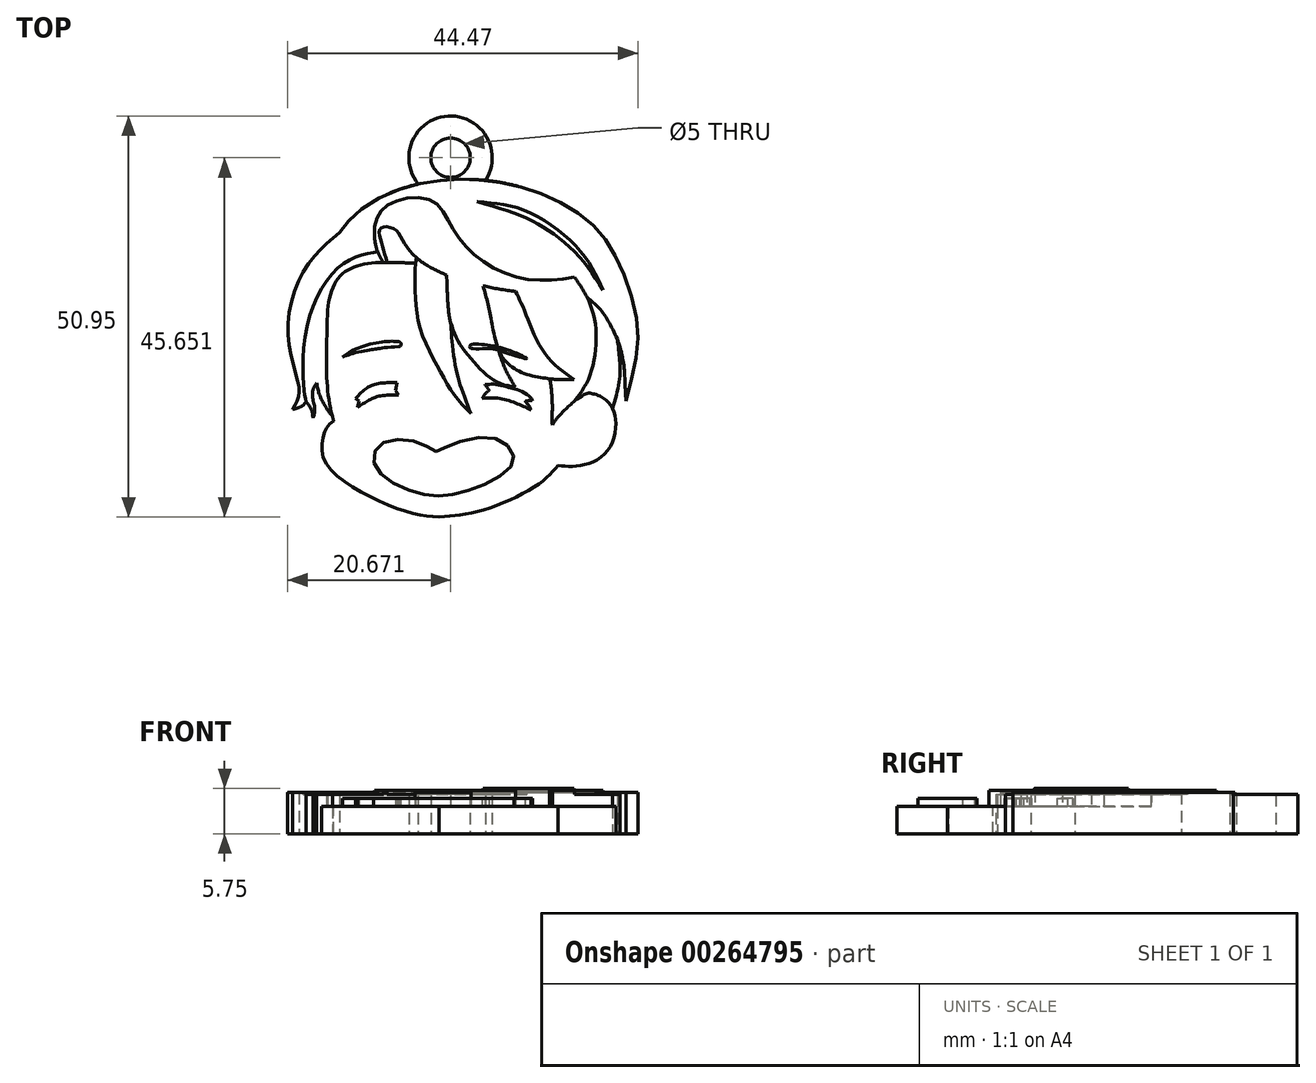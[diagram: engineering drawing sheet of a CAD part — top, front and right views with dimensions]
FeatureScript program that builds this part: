
annotation { "Feature Type Name" : "Feature", "Feature Type Description" : "" }
export const myFeature = defineFeature(function(context is Context, id is Id, definition is map)
    precondition{}
    {
        {
            var Q0;
            Q0=qCreatedBy(makeId("Top.planeOp"),FACE);
            var sketch = newSketch(context, id + "F0", { "sketchPlane" : qUnion([Q0])});
            skLineSegment(sketch, "E0", {"start": v(0, 26.14) * mm, "end": v(0, -13.86) * mm, "construction": true});
            skFitSpline(sketch, "E1", {"points": [v(-13.4, -3.41) * mm, v(-14.59, -4.9) * mm, v(-14.68, -8.16) * mm, v(-10.4, -12.17) * mm, v(-3.68, -15.06) * mm, v(0, -15.62) * mm], "startDerivative": vector(-13.93, -9.32) * mm, "endDerivative": vector(18.39, -1.5) * mm});
            skFitSpline(sketch, "E2", {"points": [v(0, -15.62) * mm, v(5.36, -14.78) * mm, v(12.63, -11.43) * mm, v(15.05, -9.1) * mm], "startDerivative": vector(14.98, 1.14) * mm, "endDerivative": vector(7.26, 8.68) * mm});
            skFitSpline(sketch, "E3", {"points": [v(15.05, -9.1) * mm, v(17.76, -9.1) * mm, v(21.2, -7.42) * mm, v(22.42, -3.41) * mm, v(21.58, -1.17) * mm, v(18.5, 0) * mm, v(15.05, -3.41) * mm, v(15.05, -4.25) * mm], "startDerivative": vector(18.97, -1.5) * mm, "endDerivative": vector(3.2, -10.24) * mm, "construction": true});
            skFitSpline(sketch, "E4", {"points": [v(14.37, -3.91) * mm, v(15.86, -2.1) * mm, v(18.5, 0) * mm, v(19.35, 0.08) * mm, v(20.48, -0.29) * mm, v(21.58, -1.17) * mm, v(22.42, -3.41) * mm, v(21.2, -7.42) * mm, v(17.76, -9.1) * mm, v(15.05, -9.1) * mm], "startDerivative": vector(9.94, 16.2) * mm, "endDerivative": vector(-21.45, 1.73) * mm});
            skFitSpline(sketch, "E5", {"points": [v(-14.19, 10.66) * mm, v(-12.54, 15.05) * mm, v(-8.76, 16.63) * mm, v(-3.04, 16.63) * mm], "startDerivative": vector(1.75, 16.5) * mm, "endDerivative": vector(16.06, -0.48) * mm});
            skFitSpline(sketch, "E6", {"points": [v(-3.04, 16.63) * mm, v(-3.04, 12.63) * mm, v(-2.33, 8) * mm, v(0, 3.15) * mm, v(1.82, 0) * mm, v(4.02, -2.5) * mm], "startDerivative": vector(-0.37, -20.1) * mm, "endDerivative": vector(13.1, -13.51) * mm});
            skFitSpline(sketch, "E7", {"points": [v(4.02, -2.5) * mm, v(2.77, 0.87) * mm, v(1.98, 3.93) * mm, v(1.56, 7.52) * mm, v(1.43, 9.09) * mm], "startDerivative": vector(-5.05, 13.03) * mm, "endDerivative": vector(-1.35, 13.2) * mm});
            skFitSpline(sketch, "E8", {"points": [v(1.43, 9.09) * mm, v(2.5, 6.55) * mm, v(4.66, 3.77) * mm, v(7.17, 1.61) * mm, v(9.69, 0.87) * mm], "startDerivative": vector(3.7, -10.7) * mm, "endDerivative": vector(11.1, -2.02) * mm});
            skFitSpline(sketch, "E9", {"points": [v(7.82, 5.39) * mm, v(9.13, 3.52) * mm, v(11.7, 2.36) * mm, v(15.14, 1.84) * mm, v(17.15, 1.84) * mm], "startDerivative": vector(4.7, -8.74) * mm, "endDerivative": vector(8.44, 0.3) * mm, "construction": true});
            skFitSpline(sketch, "E10", {"points": [v(14.01, 1.94) * mm, v(14.2, 0.87) * mm, v(14.32, -0.49) * mm, v(14.36, -2.2) * mm, v(14.37, -3.91) * mm], "startDerivative": vector(1.08, -4.56) * mm, "endDerivative": vector(1.1, -5.47) * mm});
            skFitSpline(sketch, "E11", {"points": [v(-13.4, -3.41) * mm, v(-14.31, 2.85) * mm, v(-14.19, 10.66) * mm], "startDerivative": vector(-3.96, 12.36) * mm, "endDerivative": vector(0.4, 15.4) * mm});
            skFitSpline(sketch, "E12", {"points": [v(-12.65, 20.52) * mm, v(-16.75, 16.37) * mm, v(-19.24, 8.2) * mm, v(-17.95, 1.51) * mm, v(-17.9, -0.43) * mm, v(-18.62, -1.94) * mm], "startDerivative": vector(-19.1, -15.5) * mm, "endDerivative": vector(-7.31, -11.74) * mm});
            skFitSpline(sketch, "E13", {"points": [v(-18.62, -1.94) * mm, v(-17.47, -1.53) * mm, v(-16.9, -0.98) * mm], "startDerivative": vector(2.3, 0.41) * mm, "endDerivative": vector(1.1, 1.36) * mm});
            skFitSpline(sketch, "E14", {"points": [v(-16.9, -0.98) * mm, v(-16.25, -1.94) * mm, v(-16.04, -3.02) * mm], "startDerivative": vector(1.51, -1.67) * mm, "endDerivative": vector(0.4, -2.4) * mm});
            skFitSpline(sketch, "E15", {"points": [v(-16.04, -3.02) * mm, v(-15.81, -1.94) * mm, v(-16.04, -0.8) * mm], "startDerivative": vector(0.92, 2.4) * mm, "endDerivative": vector(-0.88, 2.92) * mm});
            skFitSpline(sketch, "E16", {"points": [v(-16.04, -0.8) * mm, v(-16.04, 0.6) * mm, v(-15.58, 1.39) * mm], "startDerivative": vector(-0.2, 1.92) * mm, "endDerivative": vector(0.95, 1.57) * mm});
            skFitSpline(sketch, "E17", {"points": [v(-12.65, 20.52) * mm, v(-10.64, 22.9) * mm, v(-5.79, 25.74) * mm, v(0, 27.11) * mm, v(5.19, 27.21) * mm, v(10.8, 26.19) * mm, v(16.16, 23.92) * mm, v(20.2, 20.77) * mm, v(22.7, 16.89) * mm, v(24.9, 10.6) * mm, v(25.08, 5.27) * mm, v(23.71, -0.85) * mm], "startDerivative": vector(24.35, 34.26) * mm, "endDerivative": vector(-17.15, -63.7) * mm});
            skFitSpline(sketch, "E18", {"points": [v(22.61, 7) * mm, v(23.36, 4.37) * mm, v(23.57, 1.98) * mm, v(23.71, -0.85) * mm], "startDerivative": vector(2.65, -7.12) * mm, "endDerivative": vector(0.34, -7.37) * mm});
            skFitSpline(sketch, "E19", {"points": [v(22.61, 7) * mm, v(22.88, 4.69) * mm, v(22.88, 1.75) * mm, v(22.29, -1.24) * mm, v(22.05, -1.84) * mm], "startDerivative": vector(1.12, -8.58) * mm, "endDerivative": vector(-1.44, -3.33) * mm, "construction": true});
            skFitSpline(sketch, "E20", {"points": [v(22, -1.84) * mm, v(22.88, 1.75) * mm, v(22.88, 4.69) * mm, v(22.61, 7) * mm], "startDerivative": vector(2.87, 9.77) * mm, "endDerivative": vector(-1, 7.59) * mm});
            skFitSpline(sketch, "E21", {"points": [v(-15.58, 1.39) * mm, v(-15.19, -0.15) * mm, v(-14.34, -1.78) * mm, v(-13.58, -2.82) * mm], "startDerivative": vector(0.86, -4.54) * mm, "endDerivative": vector(2.6, -3.14) * mm});
            skFitSpline(sketch, "E22", {"points": [v(-10.64, -0.53) * mm, v(-9.31, 0.69) * mm, v(-7.93, 1.32) * mm, v(-5.39, 1.45) * mm], "startDerivative": vector(4.08, 4.14) * mm, "endDerivative": vector(7.18, -0.06) * mm});
            skFitSpline(sketch, "E23", {"points": [v(-10.64, -0.53) * mm, v(-10.2, -0.88) * mm], "startDerivative": vector(0.44, -0.35) * mm, "endDerivative": vector(0.44, -0.35) * mm});
            skFitSpline(sketch, "E24", {"points": [v(-10.2, -0.88) * mm, v(-10.4, -1.72) * mm], "startDerivative": vector(-0.2, -0.84) * mm, "endDerivative": vector(-0.2, -0.84) * mm});
            skFitSpline(sketch, "E25", {"points": [v(-10.4, -1.72) * mm, v(-9.13, -0.88) * mm, v(-7.65, -0.27) * mm, v(-5.2, -0.09) * mm], "startDerivative": vector(4.13, 2.9) * mm, "endDerivative": vector(6.8, 0.1) * mm});
            skFitSpline(sketch, "E26", {"points": [v(-5.39, 1.45) * mm, v(-5.55, 0.46) * mm], "startDerivative": vector(-0.16, -0.99) * mm, "endDerivative": vector(-0.16, -0.99) * mm});
            skFitSpline(sketch, "E27", {"points": [v(-5.55, 0.46) * mm, v(-5.2, -0.09) * mm], "startDerivative": vector(0.36, -0.54) * mm, "endDerivative": vector(0.36, -0.54) * mm});
            skFitSpline(sketch, "E28", {"points": [v(5.8, 1.2) * mm, v(7.17, 1.23) * mm, v(8.9, 0.84) * mm, v(10.2, 0.46) * mm, v(11.7, -0.53) * mm, v(11.82, -0.85) * mm], "startDerivative": vector(6.24, 0.69) * mm, "endDerivative": vector(0.25, -2.75) * mm});
            skFitSpline(sketch, "E29", {"points": [v(11.82, -0.85) * mm, v(11.29, -0.85) * mm, v(10.9, -0.92) * mm], "startDerivative": vector(-1.03, 0.04) * mm, "endDerivative": vector(-0.8, -0.2) * mm});
            skFitSpline(sketch, "E30", {"points": [v(10.9, -0.92) * mm, v(11.16, -1.19) * mm, v(11.5, -1.66) * mm, v(11.63, -2) * mm], "startDerivative": vector(0.8, -0.75) * mm, "endDerivative": vector(0.3, -1.03) * mm});
            skFitSpline(sketch, "E31", {"points": [v(11.63, -2) * mm, v(9.93, -1.23) * mm, v(7.6, -0.53) * mm, v(5.46, -0.53) * mm], "startDerivative": vector(-5.2, 2.45) * mm, "endDerivative": vector(-6.32, -0.48) * mm});
            skFitSpline(sketch, "E32", {"points": [v(5.8, 1.2) * mm, v(6.08, 0.86) * mm, v(6.35, 0.46) * mm], "startDerivative": vector(0.58, -0.66) * mm, "endDerivative": vector(0.51, -0.8) * mm});
            skFitSpline(sketch, "E33", {"points": [v(6.35, 0.46) * mm, v(5.9, 0.11) * mm, v(5.46, -0.53) * mm], "startDerivative": vector(-1.02, -0.57) * mm, "endDerivative": vector(-0.76, -1.38) * mm});
            skFitSpline(sketch, "E34", {"points": [v(-5.16, 6.68) * mm, v(-7.38, 6.62) * mm, v(-10.76, 5.64) * mm, v(-12.27, 4.73) * mm], "startDerivative": vector(-6.43, 0.3) * mm, "endDerivative": vector(-4.54, -3.28) * mm});
            skFitSpline(sketch, "E35", {"points": [v(-12.27, 4.73) * mm, v(-10.8, 5.2) * mm, v(-8.63, 5.65) * mm, v(-7.81, 5.78) * mm, v(-5.17, 6.02) * mm], "startDerivative": vector(5, 2.04) * mm, "endDerivative": vector(12.14, 0.39) * mm});
            skFitSpline(sketch, "E36", {"points": [v(-5.16, 6.68) * mm, v(-4.88, 6.48) * mm, v(-4.89, 6.15) * mm, v(-5.17, 6.02) * mm], "startDerivative": vector(1, -0.45) * mm, "endDerivative": vector(-1.03, -0.24) * mm});
            skFitSpline(sketch, "E37", {"points": [v(11.13, 4.5) * mm, v(8.62, 5.65) * mm, v(5.33, 6.3) * mm, v(3.94, 6.2) * mm, v(3.94, 5.88) * mm, v(6.12, 5.78) * mm, v(8.1, 5.39) * mm, v(11.13, 4.5) * mm]});
            skFitSpline(sketch, "E38", {"points": [v(-0.4, -7.32) * mm, v(-1.95, -6.4) * mm, v(-5.02, -5.77) * mm, v(-7.66, -6.54) * mm, v(-8.33, -8.3) * mm, v(-7.24, -10.32) * mm, v(-4.17, -12.08) * mm, v(-0.79, -12.9) * mm, v(1.96, -12.72) * mm, v(5.77, -11.45) * mm, v(8.91, -9.44) * mm, v(9.44, -7.78) * mm, v(8.1, -6.09) * mm, v(4.82, -5.52) * mm, v(0.45, -6.9) * mm, v(-0.4, -7.32) * mm]});
            skLineSegment(sketch, "E39.bottom", {"start": v(-9.61, -2.71) * mm, "end": v(-9.4, -2.71) * mm});
            skLineSegment(sketch, "E39.top", {"start": v(-9.61, -3.67) * mm, "end": v(-9.4, -3.67) * mm});
            skLineSegment(sketch, "E39.left", {"start": v(-9.61, -2.71) * mm, "end": v(-9.61, -3.67) * mm});
            skLineSegment(sketch, "E39.right", {"start": v(-9.4, -2.71) * mm, "end": v(-9.4, -3.67) * mm});
            skLineSegment(sketch, "E40.bottom", {"start": v(-8.16, -2.58) * mm, "end": v(-7.95, -2.58) * mm});
            skLineSegment(sketch, "E40.top", {"start": v(-8.16, -3.65) * mm, "end": v(-7.95, -3.65) * mm});
            skLineSegment(sketch, "E40.left", {"start": v(-8.16, -2.58) * mm, "end": v(-8.16, -3.65) * mm});
            skLineSegment(sketch, "E40.right", {"start": v(-7.95, -2.58) * mm, "end": v(-7.95, -3.65) * mm});
            skLineSegment(sketch, "E41.bottom", {"start": v(-6.18, -2.56) * mm, "end": v(-5.92, -2.56) * mm});
            skLineSegment(sketch, "E41.top", {"start": v(-6.18, -3.57) * mm, "end": v(-5.92, -3.57) * mm});
            skLineSegment(sketch, "E41.left", {"start": v(-6.18, -2.56) * mm, "end": v(-6.18, -3.57) * mm});
            skLineSegment(sketch, "E41.right", {"start": v(-5.92, -2.56) * mm, "end": v(-5.92, -3.57) * mm});
            skLineSegment(sketch, "E42.bottom", {"start": v(7.82, -3.54) * mm, "end": v(8.22, -3.54) * mm});
            skLineSegment(sketch, "E42.top", {"start": v(7.82, -4.76) * mm, "end": v(8.22, -4.76) * mm});
            skLineSegment(sketch, "E42.left", {"start": v(7.82, -3.54) * mm, "end": v(7.82, -4.76) * mm});
            skLineSegment(sketch, "E42.right", {"start": v(8.22, -3.54) * mm, "end": v(8.22, -4.76) * mm});
            skLineSegment(sketch, "E43.bottom", {"start": v(9.06, -3.54) * mm, "end": v(9.53, -3.54) * mm});
            skLineSegment(sketch, "E43.top", {"start": v(9.06, -4.83) * mm, "end": v(9.53, -4.83) * mm});
            skLineSegment(sketch, "E43.left", {"start": v(9.06, -3.54) * mm, "end": v(9.06, -4.83) * mm});
            skLineSegment(sketch, "E43.right", {"start": v(9.53, -3.54) * mm, "end": v(9.53, -4.83) * mm});
            skLineSegment(sketch, "E44.bottom", {"start": v(10.28, -3.46) * mm, "end": v(10.68, -3.46) * mm});
            skLineSegment(sketch, "E44.top", {"start": v(10.28, -4.8) * mm, "end": v(10.68, -4.8) * mm});
            skLineSegment(sketch, "E44.left", {"start": v(10.28, -3.46) * mm, "end": v(10.28, -4.8) * mm});
            skLineSegment(sketch, "E44.right", {"start": v(10.68, -3.46) * mm, "end": v(10.68, -4.8) * mm});
            skFitSpline(sketch, "E45", {"points": [v(-7.1, 16.74) * mm, v(-8, 18.64) * mm, v(-8.06, 21.96) * mm, v(-5.99, 24.33) * mm, v(-0.95, 24.57) * mm, v(1.6, 21.24) * mm, v(5.16, 17.15) * mm, v(11.1, 14.6) * mm, v(17.2, 14.84) * mm], "startDerivative": vector(-11.68, 19.6) * mm, "endDerivative": vector(41.04, 5.62) * mm});
            skFitSpline(sketch, "E46", {"points": [v(-6.64, 16.74) * mm, v(-7.45, 19.64) * mm, v(-7.45, 21.07) * mm, v(-5.7, 20.95) * mm, v(-4.15, 18.72) * mm, v(0, 15.53) * mm, v(9.49, 13.06) * mm, v(14.77, 13.24) * mm, v(17.2, 14.84) * mm], "startDerivative": vector(-7.68, 26.91) * mm, "endDerivative": vector(19.12, 16.57) * mm});
            skFitSpline(sketch, "E47", {"points": [v(-2.9, 17.32) * mm, v(-3.04, 16.63) * mm], "startDerivative": vector(-0.15, -0.7) * mm, "endDerivative": vector(-0.15, -0.7) * mm});
            skFitSpline(sketch, "E48", {"points": [v(0.94, 15.14) * mm, v(1.16, 10.73) * mm, v(1.43, 9.09) * mm], "startDerivative": vector(0.23, -8) * mm, "endDerivative": vector(0.78, -3.78) * mm});
            skLineSegment(sketch, "E49", {"start": v(5.33, 13.81) * mm, "end": v(5.13, 13.95) * mm});
            skFitSpline(sketch, "E50", {"points": [v(9.69, 0.87) * mm, v(8.23, 3.55) * mm, v(6.79, 8.4) * mm, v(6.2, 11.37) * mm, v(5.56, 13.76) * mm], "startDerivative": vector(-6.27, 9.9) * mm, "endDerivative": vector(-3.25, 11.04) * mm});
            skFitSpline(sketch, "E51", {"points": [v(9.69, 13.04) * mm, v(10.8, 10.67) * mm, v(13.33, 5.27) * mm, v(17.15, 1.84) * mm], "startDerivative": vector(4.07, -7.98) * mm, "endDerivative": vector(11.54, -8.04) * mm});
            skFitSpline(sketch, "E52", {"points": [v(7.57, 5.4) * mm, v(9.13, 3.52) * mm, v(11.7, 2.36) * mm, v(14.01, 1.94) * mm, v(15.14, 1.84) * mm, v(17.15, 1.84) * mm], "startDerivative": vector(6.28, -9.53) * mm, "endDerivative": vector(11.25, 0.15) * mm});
            skFitSpline(sketch, "E53", {"points": [v(-8.36, 17.98) * mm, v(-12.22, 16.56) * mm, v(-16.6, 9.44) * mm, v(-17.2, 0.6) * mm, v(-16.9, -0.98) * mm], "startDerivative": vector(-17.57, -3.44) * mm, "endDerivative": vector(2.33, -8.82) * mm});
            skFitSpline(sketch, "E54", {"points": [v(-7.82, 18.1) * mm, v(-8.36, 17.98) * mm], "startDerivative": vector(-0.55, -0.12) * mm, "endDerivative": vector(-0.55, -0.12) * mm});
            skFitSpline(sketch, "E55", {"points": [v(-12.65, 20.52) * mm, v(-11.54, 21.12) * mm, v(-10.45, 21.41) * mm, v(-9.17, 21.45) * mm, v(-8.2, 21.3) * mm], "startDerivative": vector(5.65, 3.37) * mm, "endDerivative": vector(3.5, -0.93) * mm});
            skFitSpline(sketch, "E56", {"points": [v(17.2, 14.84) * mm, v(19.14, 11.51) * mm, v(19.93, 7.13) * mm, v(19.04, 2.14) * mm, v(17.2, -0.89) * mm], "startDerivative": vector(9.06, -13.27) * mm, "endDerivative": vector(-8.84, -11.95) * mm});
            skFitSpline(sketch, "E57", {"points": [v(18.77, 12.31) * mm, v(20.73, 10.42) * mm, v(22.61, 7) * mm], "startDerivative": vector(4.5, -3.68) * mm, "endDerivative": vector(3.22, -6.86) * mm});
            skFitSpline(sketch, "E58", {"points": [v(4.81, 24.45) * mm, v(11.09, 23.23) * mm, v(17.96, 18.13) * mm, v(20.81, 13.21) * mm], "startDerivative": vector(19.97, -1.65) * mm, "endDerivative": vector(7.33, -16.32) * mm});
            skFitSpline(sketch, "E59", {"points": [v(4.81, 24.45) * mm, v(10.55, 22.58) * mm, v(14.29, 20.5) * mm, v(17.96, 17.25) * mm, v(20.81, 13.21) * mm], "startDerivative": vector(23.36, -6.63) * mm, "endDerivative": vector(10.67, -16.96) * mm});
            skSolve(sketch);
        }
        {
            var Q0;
            {var subQ4=sQuery(id+"F0.wireOp",EDGE,"E1");Q0=makeQuery(id+"F0.imprint","IMPRINT",FACE,{"disambiguationData":[TD([[makeQuery(id+"F0.imprint","IMPRINT",EDGE,{"derivedFrom":subQ4}),1.0]])]});}
            var Q1;
            Q1=makeQuery(id+"F0.imprint","IMPRINT",FACE,{"disambiguationData":[TD([[makeQuery(id+"F0.imprint","IMPRINT",EDGE,{"derivedFrom":sQuery(id+"F0.wireOp",EDGE,"E39.bottom")}),-1.0]])]});
            var Q2;
            Q2=makeQuery(id+"F0.imprint","IMPRINT",FACE,{"disambiguationData":[TD([[makeQuery(id+"F0.imprint","IMPRINT",EDGE,{"derivedFrom":sQuery(id+"F0.wireOp",EDGE,"E40.bottom")}),-1.0]])]});
            var Q3;
            Q3=makeQuery(id+"F0.imprint","IMPRINT",FACE,{"disambiguationData":[TD([[makeQuery(id+"F0.imprint","IMPRINT",EDGE,{"derivedFrom":sQuery(id+"F0.wireOp",EDGE,"E41.bottom")}),-1.0]])]});
            var Q4;
            Q4=makeQuery(id+"F0.imprint","IMPRINT",FACE,{"disambiguationData":[TD([[makeQuery(id+"F0.imprint","IMPRINT",EDGE,{"derivedFrom":sQuery(id+"F0.wireOp",EDGE,"E42.bottom")}),-1.0]])]});
            var Q5;
            Q5=makeQuery(id+"F0.imprint","IMPRINT",FACE,{"disambiguationData":[TD([[makeQuery(id+"F0.imprint","IMPRINT",EDGE,{"derivedFrom":sQuery(id+"F0.wireOp",EDGE,"E43.bottom")}),-1.0]])]});
            var Q6;
            Q6=makeQuery(id+"F0.imprint","IMPRINT",FACE,{"disambiguationData":[TD([[makeQuery(id+"F0.imprint","IMPRINT",EDGE,{"derivedFrom":sQuery(id+"F0.wireOp",EDGE,"E44.bottom")}),-1.0]])]});
            extrude(context, id + "F1", {"entities" : qUnion([Q0, Q1, Q2, Q3, Q4, Q5, Q6]), "depth" : 3.5 * mm, "offsetDistance" : 25 * mm});
        }
        {
            var Q0;
            Q0=makeQuery(id+"F0.imprint","IMPRINT",FACE,{"disambiguationData":[TD([[makeQuery(id+"F0.imprint","IMPRINT",EDGE,{"derivedFrom":sQuery(id+"F0.wireOp",EDGE,"E37")}),1.0]])]});
            var Q1;
            {var subQ1=sQuery(id+"F0.wireOp",EDGE,"E5");Q1=makeQuery(id+"F0.imprint","IMPRINT",FACE,{"disambiguationData":[TD([[makeQuery(id+"F0.imprint","IMPRINT",EDGE,{"derivedFrom":subQ1}),1.0]])]});}
            var Q2;
            Q2=makeQuery(id+"F0.imprint","IMPRINT",FACE,{"disambiguationData":[TD([[makeQuery(id+"F0.imprint","IMPRINT",EDGE,{"derivedFrom":sQuery(id+"F0.wireOp",EDGE,"E14")}),1.0]])]});
            var Q3;
            {var subQ0=sQuery(id+"F0.wireOp",EDGE,"E20");Q3=makeQuery(id+"F0.imprint","IMPRINT",FACE,{"disambiguationData":[TD([[makeQuery(id+"F0.imprint","IMPRINT",EDGE,{"derivedFrom":subQ0}),1.0]])]});}
            extrude(context, id + "F2", {"entities" : qUnion([Q0, Q1, Q2, Q3]), "operationType" : NewBodyOperationType.ADD, "depth" : 5 * mm, "offsetDistance" : 25 * mm});
        }
        {
            var Q0;
            Q0=makeQuery(id+"F0.imprint","IMPRINT",FACE,{"disambiguationData":[TD([[makeQuery(id+"F0.imprint","IMPRINT",EDGE,{"derivedFrom":sQuery(id+"F0.wireOp",EDGE,"E22")}),-1.0]])]});
            var Q1;
            Q1=makeQuery(id+"F0.imprint","IMPRINT",FACE,{"disambiguationData":[TD([[makeQuery(id+"F0.imprint","IMPRINT",EDGE,{"derivedFrom":sQuery(id+"F0.wireOp",EDGE,"E28")}),-1.0]])]});
            extrude(context, id + "F3", {"entities" : qUnion([Q0, Q1]), "operationType" : NewBodyOperationType.ADD, "depth" : 4.5 * mm, "offsetDistance" : 25 * mm});
        }
        {
            var Q0;
            Q0=makeQuery(id+"F0.imprint","IMPRINT",FACE,{"disambiguationData":[TD([[makeQuery(id+"F0.imprint","IMPRINT",EDGE,{"derivedFrom":sQuery(id+"F0.wireOp",EDGE,"E34")}),1.0]])]});
            var Q1;
            Q1=makeQuery(id+"F0.imprint","IMPRINT",FACE,{"disambiguationData":[TD([[makeQuery(id+"F0.imprint","IMPRINT",EDGE,{"derivedFrom":sQuery(id+"F0.wireOp",EDGE,"E38")}),1.0]])]});
            extrude(context, id + "F4", {"entities" : qUnion([Q0, Q1]), "operationType" : NewBodyOperationType.ADD, "depth" : 4.5 * mm, "offsetDistance" : 25 * mm});
        }
        {
            var Q0;
            {var subQ0=sQuery(id+"F0.wireOp",EDGE,"E45");Q0=makeQuery(id+"F0.imprint","IMPRINT",FACE,{"disambiguationData":[TD([[makeQuery(id+"F0.imprint","IMPRINT",EDGE,{"derivedFrom":subQ0}),-1.0]])]});}
            var Q1;
            {var subQ8=sQuery(id+"F0.wireOp",EDGE,"E8");Q1=makeQuery(id+"F0.imprint","IMPRINT",FACE,{"disambiguationData":[TD([[makeQuery(id+"F0.imprint","IMPRINT",EDGE,{"derivedFrom":subQ8}),1.0]])]});}
            var Q2;
            {var subQ4=sQuery(id+"F0.wireOp",EDGE,"E10");Q2=makeQuery(id+"F0.imprint","IMPRINT",FACE,{"disambiguationData":[TD([[makeQuery(id+"F0.imprint","IMPRINT",EDGE,{"derivedFrom":subQ4}),1.0]])]});}
            extrude(context, id + "F5", {"entities" : qUnion([Q0, Q1, Q2]), "operationType" : NewBodyOperationType.ADD, "depth" : 5.5 * mm, "offsetDistance" : 25 * mm});
        }
        {
            var Q0;
            Q0=makeQuery(id+"F0.imprint","IMPRINT",FACE,{"disambiguationData":[TD([[makeQuery(id+"F0.imprint","IMPRINT",EDGE,{"derivedFrom":sQuery(id+"F0.wireOp",EDGE,"E6")}),1.0]])]});
            var Q1;
            Q1=makeQuery(id+"F0.imprint","IMPRINT",FACE,{"disambiguationData":[TD([[makeQuery(id+"F0.imprint","IMPRINT",EDGE,{"derivedFrom":sQuery(id+"F0.wireOp",EDGE,"E12")}),1.0]])]});
            var Q2;
            Q2=makeQuery(id+"F0.imprint","IMPRINT",FACE,{"disambiguationData":[TD([[makeQuery(id+"F0.imprint","IMPRINT",EDGE,{"derivedFrom":sQuery(id+"F0.wireOp",EDGE,"E17")}),-1.0]])]});
            extrude(context, id + "F6", {"entities" : qUnion([Q0, Q1, Q2]), "operationType" : NewBodyOperationType.ADD, "depth" : 5.25 * mm, "offsetDistance" : 25 * mm});
        }
        {
            var Q0;
            {var subQ8=sQuery(id+"F0.wireOp",EDGE,"E51");Q0=makeQuery(id+"F0.imprint","IMPRINT",FACE,{"disambiguationData":[TD([[makeQuery(id+"F0.imprint","IMPRINT",EDGE,{"derivedFrom":subQ8}),-1.0]])]});}
            extrude(context, id + "F7", {"entities" : qUnion([Q0]), "operationType" : NewBodyOperationType.ADD, "depth" : 5.75 * mm, "offsetDistance" : 25 * mm});
        }
        {
            var Q0;
            Q0=makeQuery(id+"F0.imprint","IMPRINT",FACE,{"disambiguationData":[TD([[makeQuery(id+"F0.imprint","IMPRINT",EDGE,{"derivedFrom":sQuery(id+"F0.wireOp",EDGE,"E58")}),-1.0]])]});
            extrude(context, id + "F8", {"entities" : qUnion([Q0]), "operationType" : NewBodyOperationType.ADD, "depth" : 5.5 * mm, "offsetDistance" : 25 * mm});
        }
        {
            var Q0;
            Q0=qCreatedBy(makeId("Top.planeOp"),FACE);
            var sketch = newSketch(context, id + "F9", { "sketchPlane" : qUnion([Q0])});
            skCircle(sketch, "E60", {"center": v(1.43, 30.03) * mm, "radius": 5.3 * mm});
            skCircle(sketch, "E61", {"center": v(1.43, 30.03) * mm, "radius": 2.5 * mm});
            skLineSegment(sketch, "E62", {"start": v(-1.07, 30.03) * mm, "end": v(3.93, 30.03) * mm, "construction": true});
            skSolve(sketch);
        }
        {
            var Q0;
            Q0=makeQuery(id+"F9.imprint","IMPRINT",FACE,{"disambiguationData":[TD([[makeQuery(id+"F9.imprint","IMPRINT",EDGE,{"derivedFrom":sQuery(id+"F9.wireOp",EDGE,"E60")}),1.0]])]});
            extrude(context, id + "F10", {"entities" : qUnion([Q0]), "operationType" : NewBodyOperationType.ADD, "depth" : 5 * mm, "offsetDistance" : 25 * mm});
        }
    });
